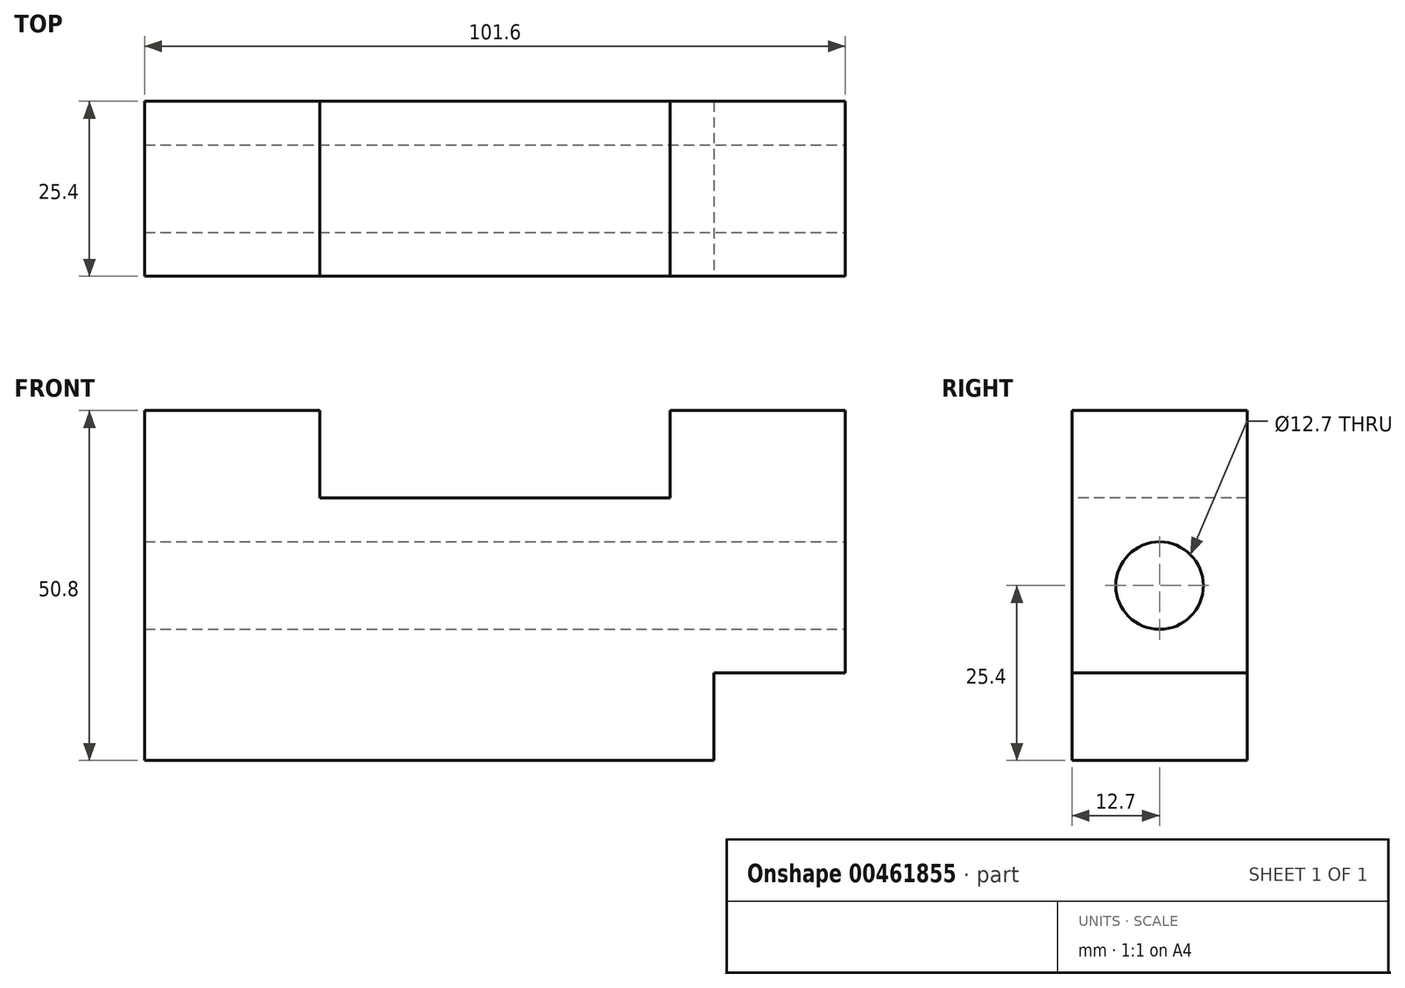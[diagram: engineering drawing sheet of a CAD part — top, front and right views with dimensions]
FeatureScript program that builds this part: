
annotation { "Feature Type Name" : "Feature", "Feature Type Description" : "" }
export const myFeature = defineFeature(function(context is Context, id is Id, definition is map)
    precondition{}
    {
        {
            var Q0;
            Q0=qCreatedBy(makeId("Front.planeOp"),FACE);
            var sketch = newSketch(context, id + "F0", { "sketchPlane" : qUnion([Q0])});
            skLineSegment(sketch, "E0.bottom", {"start": v(50.8, 25.4) * mm, "end": v(-50.8, 25.4) * mm});
            skLineSegment(sketch, "E0.top", {"start": v(50.8, -25.4) * mm, "end": v(-50.8, -25.4) * mm});
            skLineSegment(sketch, "E0.left", {"start": v(50.8, 25.4) * mm, "end": v(50.8, -25.4) * mm});
            skLineSegment(sketch, "E0.right", {"start": v(-50.8, 25.4) * mm, "end": v(-50.8, -25.4) * mm});
            skPoint(sketch, "E0.middle", {"position": v(0, 0) * mm});
            skSolve(sketch);
        }
        {
            var Q0;
            Q0 = qSketchRegion(id + "F0", true);
            extrude(context, id + "F1", {"entities" : qUnion([Q0]), "depth" : 25.4 * mm});
        }
        {
            var Q0;
            Q0=makeQuery(id+"F1.opExtrude","CAP_FACE",FACE,{"disambiguationData":[OSD([sQuery(id+"F0.wireOp",EDGE,"E0.bottom"),sQuery(id+"F0.wireOp",EDGE,"E0.top"),sQuery(id+"F0.wireOp",EDGE,"E0.left"),sQuery(id+"F0.wireOp",EDGE,"E0.right")])],"isStart":false});
            var sketch = newSketch(context, id + "F2", { "sketchPlane" : qUnion([Q0])});
            skLineSegment(sketch, "E1.bottom", {"start": v(-25.4, 25.4) * mm, "end": v(25.4, 25.4) * mm});
            skLineSegment(sketch, "E1.top", {"start": v(-25.4, 12.7) * mm, "end": v(25.4, 12.7) * mm});
            skLineSegment(sketch, "E1.left", {"start": v(-25.4, 25.4) * mm, "end": v(-25.4, 12.7) * mm});
            skLineSegment(sketch, "E1.right", {"start": v(25.4, 25.4) * mm, "end": v(25.4, 12.7) * mm});
            skSolve(sketch);
        }
        {
            var Q0;
            Q0=makeQuery(id+"F2.imprint","IMPRINT",FACE,{"disambiguationData":[TD([[makeQuery(id+"F2.imprint","IMPRINT",EDGE,{"derivedFrom":sQuery(id+"F2.wireOp",EDGE,"E1.bottom")}),1.0]])]});
            extrude(context, id + "F3", {"entities" : qUnion([Q0]), "operationType" : NewBodyOperationType.REMOVE, "endBound" : BoundingType.THROUGH_ALL, "oppositeDirection" : true, "depth" : 25.4 * mm});
        }
        {
            var Q0;
            Q0=makeQuery(id+"F1.opExtrude","CAP_FACE",FACE,{"disambiguationData":[OSD([sQuery(id+"F0.wireOp",EDGE,"E0.bottom"),sQuery(id+"F0.wireOp",EDGE,"E0.top"),sQuery(id+"F0.wireOp",EDGE,"E0.left"),sQuery(id+"F0.wireOp",EDGE,"E0.right")])],"isStart":false});
            var sketch = newSketch(context, id + "F4", { "sketchPlane" : qUnion([Q0])});
            skLineSegment(sketch, "E2.bottom", {"start": v(31.75, -25.4) * mm, "end": v(50.8, -25.4) * mm});
            skLineSegment(sketch, "E2.top", {"start": v(31.75, -12.7) * mm, "end": v(50.8, -12.7) * mm});
            skLineSegment(sketch, "E2.left", {"start": v(31.75, -25.4) * mm, "end": v(31.75, -12.7) * mm});
            skLineSegment(sketch, "E2.right", {"start": v(50.8, -25.4) * mm, "end": v(50.8, -12.7) * mm});
            skSolve(sketch);
        }
        {
            var Q0;
            Q0=makeQuery(id+"F4.imprint","IMPRINT",FACE,{"disambiguationData":[TD([[makeQuery(id+"F4.imprint","IMPRINT",EDGE,{"derivedFrom":sQuery(id+"F4.wireOp",EDGE,"E2.bottom")}),-1.0]])]});
            extrude(context, id + "F5", {"entities" : qUnion([Q0]), "operationType" : NewBodyOperationType.REMOVE, "endBound" : BoundingType.THROUGH_ALL, "oppositeDirection" : true, "depth" : 25.4 * mm});
        }
        {
            var Q0;
            Q0=makeQuery(id+"F1.opExtrude","SWEPT_FACE",FACE,{"disambiguationData":[OSD([sQuery(id+"F0.wireOp",EDGE,"E0.left")])]});
            var sketch = newSketch(context, id + "F6", { "sketchPlane" : qUnion([Q0])});
            skCircle(sketch, "E3", {"center": v(-12.7, 0) * mm, "radius": 6.35 * mm});
            skSolve(sketch);
        }
        {
            var Q0;
            Q0=makeQuery(id+"F6.imprint","IMPRINT",FACE,{"disambiguationData":[TD([[makeQuery(id+"F6.imprint","IMPRINT",EDGE,{"derivedFrom":sQuery(id+"F6.wireOp",EDGE,"E3")}),1.0]])]});
            extrude(context, id + "F7", {"entities" : qUnion([Q0]), "operationType" : NewBodyOperationType.REMOVE, "endBound" : BoundingType.THROUGH_ALL, "oppositeDirection" : true, "depth" : 25.4 * mm});
        }
    });
